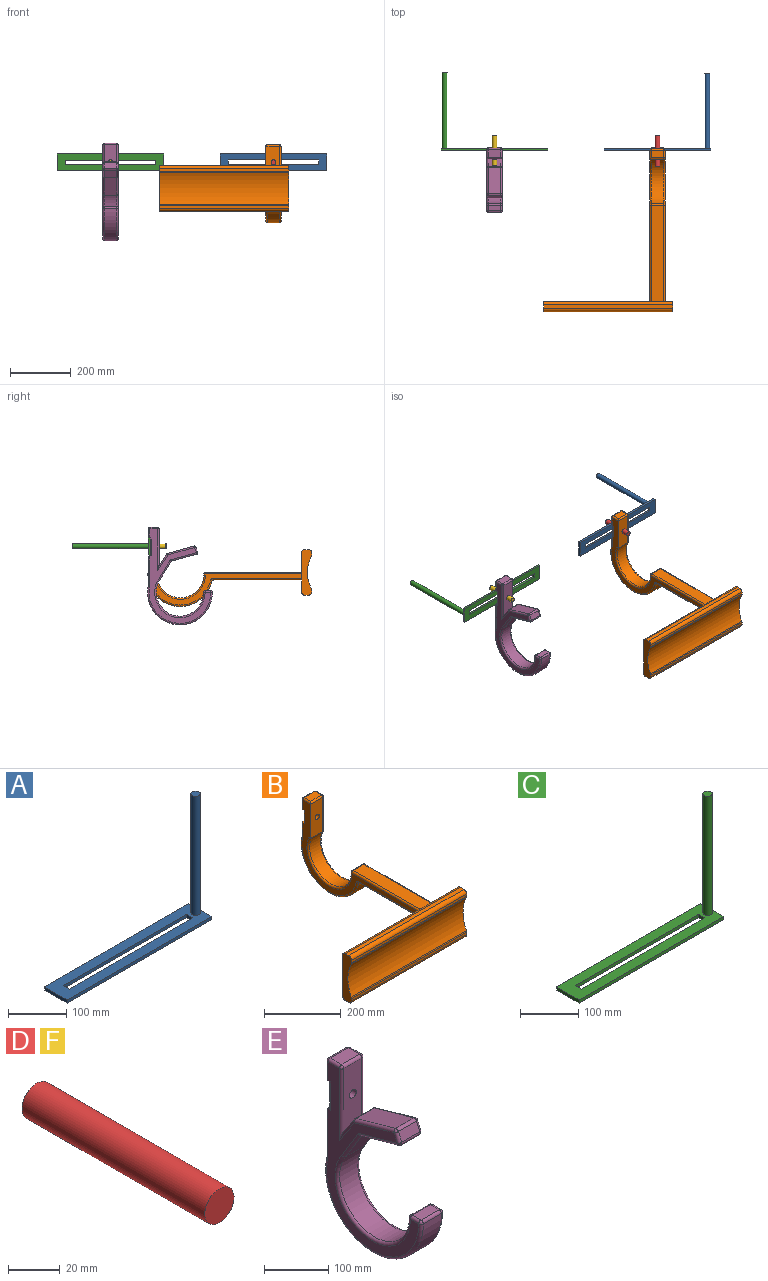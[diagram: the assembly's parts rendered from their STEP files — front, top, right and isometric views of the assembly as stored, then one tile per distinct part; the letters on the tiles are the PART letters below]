
ASSEMBLY  parts=6 mates=4
PART A: 12 faces, bbox 350x54.6x256.5 mm
  f0: plane 350x54.58mm, normal (0,0,1), area 14418.2mm2, adj f1,f3,f4,f5,f6,f7,f8,f9
  f1: plane 350x6.45mm, normal (0,-1,0), area 2257.7mm2, adj f0,f2,f4,f5
  f2: plane 350x54.58mm, normal (0,0,-1), area 14619.2mm2, adj f1,f3,f4,f5,f6,f7,f8,f9
  f3: plane 350x6.45mm, normal (0,1,0), area 2257.7mm2, adj f0,f2,f4,f5
  f4: plane 54.58x6.45mm, normal (1,0,0), area 352.1mm2, adj f0,f1,f2,f3
  f5: plane 54.58x6.45mm, normal (-1,0,0), area 352.1mm2, adj f0,f1,f2,f3
  f6: plane 15x6.45mm, normal (1,0,0), area 96.8mm2, adj f0,f2,f7,f9
  f7: plane 298.97x6.45mm, normal (0,1,0), area 1928.6mm2, adj f0,f2,f6,f8
  f8: plane 15x6.45mm, normal (-1,0,0), area 96.8mm2, adj f0,f2,f7,f9
  f9: plane 298.97x6.45mm, normal (0,-1,0), area 1928.6mm2, adj f0,f2,f6,f8
  f10: cylinder r=8mm len=250mm, axis (0,0,-1), area 12566.4mm2, adj f0,f11
  f11: plane 16x16mm, normal (0,0,1), area 201.1mm2, adj f10
PART B: 68 faces, bbox 425x547.6x264.4 mm
  f0: plane 41.08x40mm, normal (0,1,0), area 1643.3mm2, adj f29,f36,f40,f42
  f1: plane 500.7x245.65mm, normal (-1,0,0), area 13483.1mm2, adj f11,f25,f26,f28,f29,f33,f37,f39
  f2: plane 500.7x245.65mm, normal (1,0,0), area 12934.7mm2, adj f11,f25,f28,f29,f31,f32,f35,f36
  f3: cylinder r=7.5mm len=27.51mm, axis (0,-1,0), area 1296.5mm2, adj f26,f30
  f4: plane 425x7.79mm, normal (0,-1,0), area 3309mm2, adj f13,f16,f19,f22
  f5: plane 290x40mm, normal (0,0,-1), area 11600mm2, adj f11,f31,f33,f34
  f6: plane 316.33x40mm, normal (0,0,1), area 12653.2mm2, adj f11,f44,f50,f51
  f7: cylinder r=106.68mm len=210.82mm, axis (-1,0,0), area 13645.9mm2, adj f34,f35,f39,f40
  f8: cylinder r=77.9mm len=155.57mm, axis (-1,0,0), area 10978.7mm2, adj f10,f43,f48,f49
  f9: plane 40x6.31mm, normal (0,1,0), area 252.3mm2, adj f45,f48,f51,f54
  f10: plane 42.72x0.17mm, normal (0,-0.55,0.83), area 7.8mm2, adj f8,f25,f43,f49
  f11: plane 425x130mm, normal (0,1,0), area 54021.5mm2, adj f1,f2,f5,f6,f13,f16,f21,f23
  f12: plane 425x7.79mm, normal (0,-1,0), area 3309mm2, adj f13,f16,f18,f20
  f13: plane 150x33.08mm, normal (-1,0,0), area 3853.4mm2, adj f4,f11,f12,f14,f15,f17,f18,f19
  f14: plane 425x13.08mm, normal (0,0,1), area 5558.4mm2, adj f13,f16,f22,f23
  f15: plane 425x13.08mm, normal (0,0,-1), area 5558.4mm2, adj f13,f16,f20,f21
  f16: plane 150x33.08mm, normal (1,0,0), area 3853.4mm2, adj f4,f11,f12,f14,f15,f17,f18,f19
  f17: cylinder r=115.34mm len=425mm, axis (1,0,0), area 46473mm2, adj f13,f16,f18,f19
  f18: cylinder r=10mm len=425mm, axis (1,0,0), area 2014.7mm2, adj f12,f13,f16,f17
  f19: cylinder r=10mm len=425mm, axis (1,0,0), area 2014.7mm2, adj f4,f13,f16,f17
  f20: cylinder r=10mm len=425mm, axis (-1,0,0), area 6675.9mm2, adj f12,f13,f15,f16
  f21: cylinder r=10mm len=425mm, axis (1,0,0), area 6675.9mm2, adj f11,f13,f15,f16
  f22: cylinder r=10mm len=425mm, axis (1,0,0), area 6675.9mm2, adj f4,f13,f14,f16
  f23: cylinder r=10mm len=425mm, axis (-1,0,0), area 6675.9mm2, adj f11,f13,f14,f16
  f24: plane 40x26.99mm, normal (0,1,0), area 1079.5mm2, adj f56,f57,f59,f60
  f25: plane 50x6.79mm, normal (0,-0.18,-0.98), area 55.4mm2, adj f1,f2,f10,f26,f43,f49,f65
  f26: plane 109.23x45mm, normal (0,-1,0), area 4738.7mm2, adj f1,f3,f25,f63,f65
  f27: plane 40x23.43mm, normal (0,0,1), area 937.2mm2, adj f55,f60,f62,f63
  f28: plane 50x5.92mm, normal (0,0,-1), area 56.6mm2, adj f1,f2,f30,f57,f66,f67
  f29: plane 50x10.92mm, normal (0,0,1), area 295.9mm2, adj f0,f1,f2,f30,f36,f42,f66,f67
  f30: plane 40.56x40mm, normal (0,1,0), area 1445.7mm2, adj f3,f28,f29,f66,f67
  f31: cylinder r=5mm len=290mm, axis (0,-1,0), area 2277.7mm2, adj f2,f5,f11,f32
  f32: torus R=10mm, axis (1,0,0), area 72.4mm2, adj f2,f31,f34,f35
  f33: cylinder r=5mm len=290mm, axis (0,1,0), area 2277.7mm2, adj f1,f5,f11,f37
  f34: cylinder r=5mm len=40mm, axis (-1,0,0), area 270.4mm2, adj f5,f7,f32,f37
  f35: torus R=101.68mm, axis (1,0,0), area 2633.7mm2, adj f2,f7,f32,f38
  f36: cylinder r=5mm len=41.08mm, axis (0,0,-1), area 322.7mm2, adj f0,f2,f29,f38
  f37: torus R=10mm, axis (1,0,0), area 72.4mm2, adj f1,f33,f34,f39
  f38: torus R=10mm, axis (1,0,0), area 14.7mm2, adj f2,f35,f36,f40
  f39: torus R=101.68mm, axis (1,0,0), area 2633.7mm2, adj f1,f7,f37,f41
  f40: cylinder r=5mm len=40mm, axis (-1,0,0), area 55mm2, adj f0,f7,f38,f41
  f41: torus R=10mm, axis (1,0,0), area 14.7mm2, adj f1,f39,f40,f42
  f42: cylinder r=5mm len=41.08mm, axis (0,0,1), area 322.7mm2, adj f0,f1,f29,f41
  f43: torus R=82.9mm, axis (1,0,0), area 2196.5mm2, adj f1,f8,f10,f25,f46
  f44: cylinder r=5mm len=316.33mm, axis (0,-1,0), area 2484.5mm2, adj f1,f6,f11,f47
  f45: cylinder r=5mm len=6.31mm, axis (0,0,-1), area 49.5mm2, adj f1,f9,f46,f47
  f46: torus R=10mm, axis (1,0,0), area 4.1mm2, adj f1,f43,f45,f48
  f47: sphere r=5mm, area 39.3mm2, adj f44,f45,f51
  f48: cylinder r=5mm len=40mm, axis (-1,0,0), area 15.3mm2, adj f8,f9,f46,f52
  f49: torus R=82.9mm, axis (1,0,0), area 2196.5mm2, adj f2,f8,f10,f25,f52
  f50: cylinder r=5mm len=316.33mm, axis (0,1,0), area 2484.5mm2, adj f2,f6,f11,f53
  f51: cylinder r=5mm len=40mm, axis (-1,0,0), area 314.2mm2, adj f6,f9,f47,f53
  f52: torus R=10mm, axis (1,0,0), area 4.1mm2, adj f2,f48,f49,f54
  f53: sphere r=5mm, area 39.3mm2, adj f50,f51,f54
  f54: cylinder r=5mm len=6.31mm, axis (0,0,1), area 49.5mm2, adj f2,f9,f52,f53
  f55: cylinder r=5mm len=23.43mm, axis (0,1,0), area 184mm2, adj f2,f27,f58,f64
  f56: cylinder r=5mm len=31.99mm, axis (0,0,-1), area 237mm2, adj f2,f24,f57,f58
  f57: cylinder r=5mm len=50mm, axis (1,0,0), area 364.2mm2, adj f24,f28,f56,f59
  f58: sphere r=5mm, area 39.3mm2, adj f55,f56,f60
  f59: cylinder r=5mm len=31.99mm, axis (0,0,1), area 237mm2, adj f1,f24,f57,f61
  f60: cylinder r=5mm len=40mm, axis (-1,0,0), area 314.2mm2, adj f24,f27,f58,f61
  f61: sphere r=5mm, area 39.3mm2, adj f59,f60,f62
  f62: cylinder r=5mm len=28.43mm, axis (0,-1,0), area 209mm2, adj f1,f27,f61,f63
  f63: cylinder r=5mm len=45mm, axis (-1,0,0), area 339.2mm2, adj f26,f27,f62,f64
  f64: sphere r=5mm, area 39.3mm2, adj f55,f63,f65
  f65: cylinder r=5mm len=110.15mm, axis (0,0,1), area 860.5mm2, adj f2,f25,f26,f64
  f66: cylinder r=5mm len=40.56mm, axis (0,0,-1), area 318.6mm2, adj f1,f28,f29,f30
  f67: cylinder r=5mm len=40.56mm, axis (0,0,1), area 318.6mm2, adj f2,f28,f29,f30
PART C: 12 faces, bbox 350x54.6x256.5 mm
  f0: plane 350x54.58mm, normal (0,0,1), area 14418.2mm2, adj f1,f3,f4,f5,f6,f7,f8,f9
  f1: plane 350x6.45mm, normal (0,-1,0), area 2257.7mm2, adj f0,f2,f4,f5
  f2: plane 350x54.58mm, normal (0,0,-1), area 14619.2mm2, adj f1,f3,f4,f5,f6,f7,f8,f9
  f3: plane 350x6.45mm, normal (0,1,0), area 2257.7mm2, adj f0,f2,f4,f5
  f4: plane 54.58x6.45mm, normal (1,0,0), area 352.1mm2, adj f0,f1,f2,f3
  f5: plane 54.58x6.45mm, normal (-1,0,0), area 352.1mm2, adj f0,f1,f2,f3
  f6: plane 15x6.45mm, normal (1,0,0), area 96.8mm2, adj f0,f2,f7,f9
  f7: plane 298.97x6.45mm, normal (0,1,0), area 1928.6mm2, adj f0,f2,f6,f8
  f8: plane 15x6.45mm, normal (-1,0,0), area 96.8mm2, adj f0,f2,f7,f9
  f9: plane 298.97x6.45mm, normal (0,-1,0), area 1928.6mm2, adj f0,f2,f6,f8
  f10: cylinder r=8mm len=250mm, axis (0,0,-1), area 12566.4mm2, adj f0,f11
  f11: plane 16x16mm, normal (0,0,1), area 201.1mm2, adj f10
PART D: 3 faces, bbox 16x100x16 mm
  f0: cylinder r=8mm len=100mm, axis (0,1,0), area 5026.5mm2, adj f1,f2
  f1: plane 16x16mm, normal (0,-1,0), area 201.1mm2, adj f0
  f2: plane 16x16mm, normal (0,1,0), area 201.1mm2, adj f0
PART E: 70 faces, bbox 50x230.9x330.6 mm
  f0: plane 40x37.03mm, normal (0,0.83,0.55), area 1774.7mm2, adj f10,f49,f58,f59
  f1: cylinder r=77.9mm len=155.8mm, axis (1,0,0), area 11671.8mm2, adj f2,f30,f34,f35
  f2: plane 59.19x40mm, normal (0,-0.85,-0.52), area 2775.1mm2, adj f1,f3,f36,f37
  f3: plane 84.21x40mm, normal (0,-0.27,-0.96), area 3493.8mm2, adj f2,f38,f39,f40
  f4: plane 40x17.16mm, normal (0,-0.92,0.39), area 746.8mm2, adj f39,f43,f44,f45
  f5: plane 87.2x40mm, normal (0,0.27,0.96), area 3626.1mm2, adj f44,f48,f49,f50
  f6: cylinder r=106.68mm len=213.37mm, axis (1,0,0), area 14418.3mm2, adj f20,f24,f25,f26
  f7: plane 40x18.78mm, normal (0,0,1), area 751.3mm2, adj f25,f29,f30,f31
  f8: plane 311.77x203.37mm, normal (-1,0,0), area 13032.6mm2, adj f13,f15,f21,f23,f26,f31,f35,f37
  f9: plane 311.77x203.37mm, normal (1,0,0), area 13032.6mm2, adj f13,f15,f19,f22,f24,f29,f34,f36
  f10: plane 121.11x40mm, normal (0,-1,0), area 4667.7mm2, adj f0,f17,f62,f63,f67
  f11: plane 40x25.17mm, normal (0,0,1), area 1006.8mm2, adj f56,f61,f64,f67
  f12: plane 40x30.08mm, normal (0,1,0), area 1203.4mm2, adj f51,f52,f55,f56
  f13: plane 50x6.45mm, normal (0,0,-1), area 83.2mm2, adj f8,f9,f14,f51,f68,f69
  f14: plane 54.58x40mm, normal (0,1,0), area 2006.5mm2, adj f13,f15,f17,f68,f69
  f15: plane 50x6.45mm, normal (0,0,1), area 83.2mm2, adj f8,f9,f14,f18,f68,f69
  f16: plane 89.98x40mm, normal (0,1,0), area 3599.1mm2, adj f18,f19,f20,f21
  f17: cylinder r=7.5mm len=28.72mm, axis (0,-1,0), area 1353.3mm2, adj f10,f14
  f18: cylinder r=5mm len=50mm, axis (-1,0,0), area 364.2mm2, adj f15,f16,f19,f21
  f19: cylinder r=5mm len=94.98mm, axis (0,0,-1), area 731.7mm2, adj f9,f16,f18,f22
  f20: cylinder r=5mm len=40mm, axis (1,0,0), area 46mm2, adj f6,f16,f22,f23
  f21: cylinder r=5mm len=94.98mm, axis (0,0,1), area 731.7mm2, adj f8,f16,f18,f23
  f22: torus R=10mm, axis (1,0,0), area 12.3mm2, adj f9,f19,f20,f24
  f23: torus R=10mm, axis (1,0,0), area 12.3mm2, adj f8,f20,f21,f26
  f24: torus R=101.68mm, axis (1,0,0), area 2782.8mm2, adj f6,f9,f22,f27
  f25: cylinder r=5mm len=40mm, axis (1,0,0), area 312.7mm2, adj f6,f7,f27,f28
  f26: torus R=101.68mm, axis (1,0,0), area 2782.8mm2, adj f6,f8,f23,f28
  f27: sphere r=5mm, area 39.1mm2, adj f24,f25,f29
  f28: sphere r=5mm, area 39.1mm2, adj f25,f26,f31
  f29: cylinder r=5mm len=18.78mm, axis (0,-1,0), area 147.5mm2, adj f7,f9,f27,f32
  f30: cylinder r=5mm len=40mm, axis (1,0,0), area 316mm2, adj f1,f7,f32,f33
  f31: cylinder r=5mm len=18.78mm, axis (0,1,0), area 147.5mm2, adj f7,f8,f28,f33
  f32: sphere r=5mm, area 39.5mm2, adj f29,f30,f34
  f33: sphere r=5mm, area 39.4mm2, adj f30,f31,f35
  f34: torus R=82.9mm, axis (1,0,0), area 2344.8mm2, adj f1,f9,f32,f36
  f35: torus R=82.9mm, axis (1,0,0), area 2344.8mm2, adj f1,f8,f33,f37
  f36: cylinder r=5mm len=63.48mm, axis (0,0.52,-0.85), area 550.1mm2, adj f2,f9,f34,f38
  f37: cylinder r=5mm len=63.48mm, axis (0,-0.52,0.85), area 550.1mm2, adj f2,f8,f35,f40
  f38: cylinder r=5mm len=87.45mm, axis (0,0.96,-0.27), area 691.7mm2, adj f3,f9,f36,f41
  f39: cylinder r=5mm len=40mm, axis (1,0,0), area 341.4mm2, adj f3,f4,f41,f42
  f40: cylinder r=5mm len=87.45mm, axis (0,-0.96,0.27), area 691.7mm2, adj f3,f8,f37,f42
  f41: sphere r=5mm, area 42.7mm2, adj f38,f39,f43
  f42: sphere r=5mm, area 42.7mm2, adj f39,f40,f45
  f43: cylinder r=5mm len=19.13mm, axis (0,-0.39,-0.92), area 146.6mm2, adj f4,f9,f41,f46
  f44: cylinder r=5mm len=40mm, axis (1,0,0), area 288.6mm2, adj f4,f5,f46,f47
  f45: cylinder r=5mm len=19.13mm, axis (0,0.39,0.92), area 146.6mm2, adj f4,f8,f42,f47
  f46: sphere r=5mm, area 36.1mm2, adj f43,f44,f48
  f47: sphere r=5mm, area 36.1mm2, adj f44,f45,f50
  f48: cylinder r=5mm len=88.57mm, axis (0,-0.96,0.27), area 712mm2, adj f5,f9,f46,f53
  f49: cylinder r=5mm len=40mm, axis (1,0,0), area 142.2mm2, adj f0,f5,f53,f54
  f50: cylinder r=5mm len=88.57mm, axis (0,0.96,-0.27), area 712mm2, adj f5,f8,f47,f54
  f51: cylinder r=5mm len=50mm, axis (-1,0,0), area 364.2mm2, adj f12,f13,f52,f55
  f52: cylinder r=5mm len=35.08mm, axis (0,0,-1), area 261.3mm2, adj f9,f12,f51,f57
  f53: sphere r=5mm, area 17.8mm2, adj f48,f49,f58
  f54: sphere r=5mm, area 17.8mm2, adj f49,f50,f59
  f55: cylinder r=5mm len=35.08mm, axis (0,0,1), area 261.3mm2, adj f8,f12,f51,f60
  f56: cylinder r=5mm len=40mm, axis (-1,0,0), area 314.2mm2, adj f11,f12,f57,f60
  f57: sphere r=5mm, area 39.3mm2, adj f52,f56,f61
  f58: cylinder r=5mm len=53.69mm, axis (0,-0.55,0.83), area 396mm2, adj f0,f9,f53,f62
  f59: cylinder r=5mm len=53.69mm, axis (0,0.55,-0.83), area 396mm2, adj f0,f8,f54,f63
  f60: sphere r=5mm, area 39.3mm2, adj f55,f56,f64
  f61: cylinder r=5mm len=25.17mm, axis (0,1,0), area 197.7mm2, adj f9,f11,f57,f65
  f62: cylinder r=5mm len=137.77mm, axis (0,0,1), area 998.7mm2, adj f9,f10,f58,f65
  f63: cylinder r=5mm len=137.77mm, axis (0,0,-1), area 998.7mm2, adj f8,f10,f59,f66
  f64: cylinder r=5mm len=25.17mm, axis (0,-1,0), area 197.7mm2, adj f8,f11,f60,f66
  f65: sphere r=5mm, area 39.3mm2, adj f61,f62,f67
  f66: sphere r=5mm, area 39.3mm2, adj f63,f64,f67
  f67: cylinder r=5mm len=40mm, axis (-1,0,0), area 314.2mm2, adj f10,f11,f65,f66
  f68: cylinder r=5mm len=54.58mm, axis (0,0,1), area 428.7mm2, adj f8,f13,f14,f15
  f69: cylinder r=5mm len=54.58mm, axis (0,0,-1), area 428.7mm2, adj f9,f13,f14,f15
PART F: same geometry as D
PLACE A rot(axis=(-1,0,0),90deg) t=(-641.28,70.64,-139.06)mm
PLACE B t=(-691.28,-116.65,-1642.74)mm
PLACE C rot(axis=(0,0.71,0.71),180deg) t=(-651.72,369.72,-112.04)mm
PLACE D rot(axis=(1,0,0),0deg) t=(-425.93,116.25,-150.55)mm
PLACE E t=(-767.72,-115.29,-1703.03)mm
PLACE F t=(-962.36,118.34,-150.67)mm
MATE fastened A.f2 <-> D.f0  axis (0,-1,0) through (-466.28,66.25,-125.49)mm
MATE fastened F.f0 <-> E.f17  axis (0,1,0) through (-1002.72,68.34,-125.61)mm
MATE fastened D.f0 <-> B.f3  axis (0,1,0) through (-466.28,66.25,-125.49)mm
MATE fastened C.f2 <-> F.f0  axis (0,-1,0) through (-1002.72,68.34,-125.61)mm
